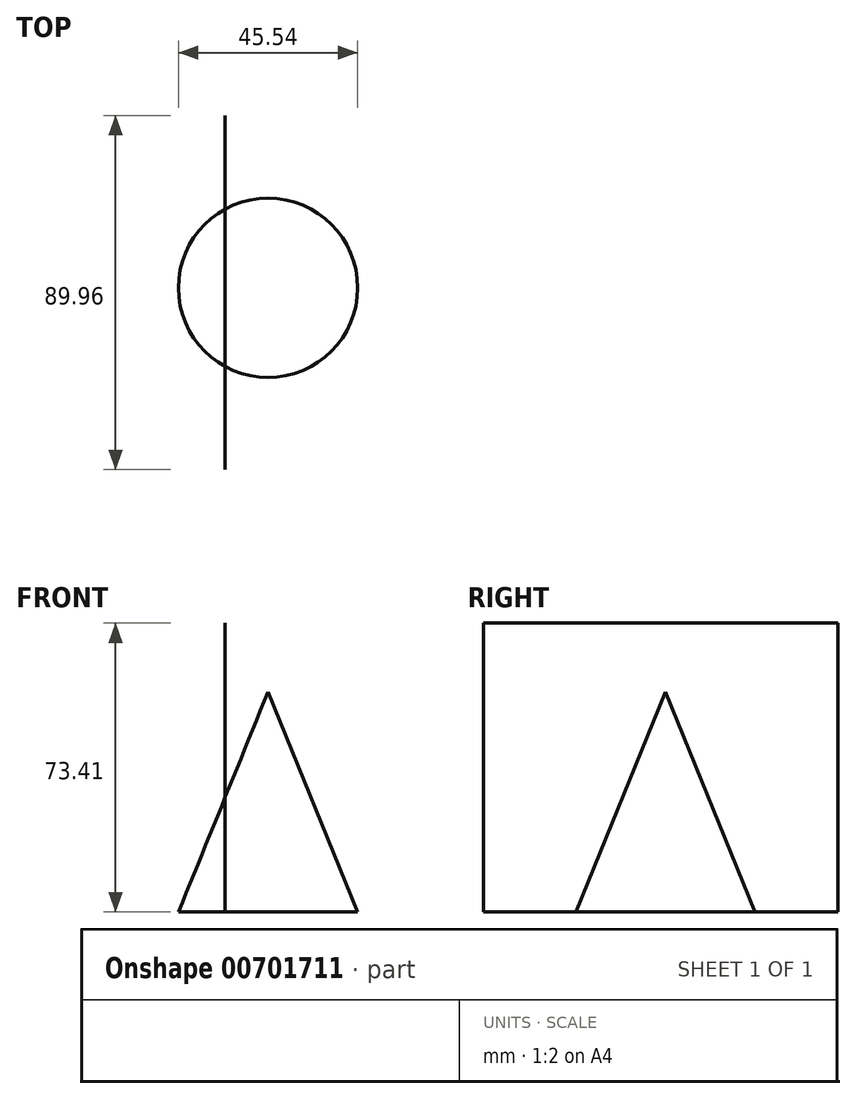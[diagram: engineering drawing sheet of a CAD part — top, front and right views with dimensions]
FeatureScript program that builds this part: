
annotation { "Feature Type Name" : "Feature", "Feature Type Description" : "" }
export const myFeature = defineFeature(function(context is Context, id is Id, definition is map)
    precondition{}
    {
        {
            var Q0;
            Q0=qCreatedBy(makeId("Front.planeOp"),FACE);
            var sketch = newSketch(context, id + "F0", { "sketchPlane" : qUnion([Q0])});
            skLineSegment(sketch, "E0", {"start": v(0, 0) * mm, "end": v(-22.77, 0) * mm});
            skLineSegment(sketch, "E1", {"start": v(-22.77, 0) * mm, "end": v(0, 55.95) * mm});
            skLineSegment(sketch, "E2", {"start": v(0, 55.95) * mm, "end": v(0, 0) * mm});
            skSolve(sketch);
        }
        {
            var Q0;
            Q0 = qSketchRegion(id + "F0", true);
            var Q1;
            Q1=sQuery(id+"F0.wireOp",EDGE,"E1");
            var Q2;
            Q2=sQuery(id+"F0.wireOp",EDGE,"E0");
            var Q3;
            Q3=sQuery(id+"F0.wireOp",EDGE,"E2");
            revolve(context, id + "F1", {"bodyType" : ToolBodyType.SURFACE, "surfaceOperationType" : NewSurfaceOperationType.NEW, "entities" : qUnion([Q0]), "surfaceEntities" : qUnion([Q1, Q2]), "axis" : qUnion([Q3]), "revolveType" : RevolveType.FULL});
        }
        {
            var Q0;
            Q0=qCreatedBy(makeId("Top.planeOp"),FACE);
            var sketch = newSketch(context, id + "F2", { "sketchPlane" : qUnion([Q0])});
            skLineSegment(sketch, "E3", {"start": v(-10.97, 43.78) * mm, "end": v(-10.97, -46.18) * mm});
            skSolve(sketch);
        }
        {
            var Q0;
            Q0=sQuery(id+"F2.wireOp",EDGE,"E3");
            extrude(context, id + "F3", {"bodyType" : ToolBodyType.SURFACE, "surfaceEntities" : qUnion([Q0]), "depth" : 73.4 * mm, "offsetDistance" : 25.4 * mm});
        }
    });
